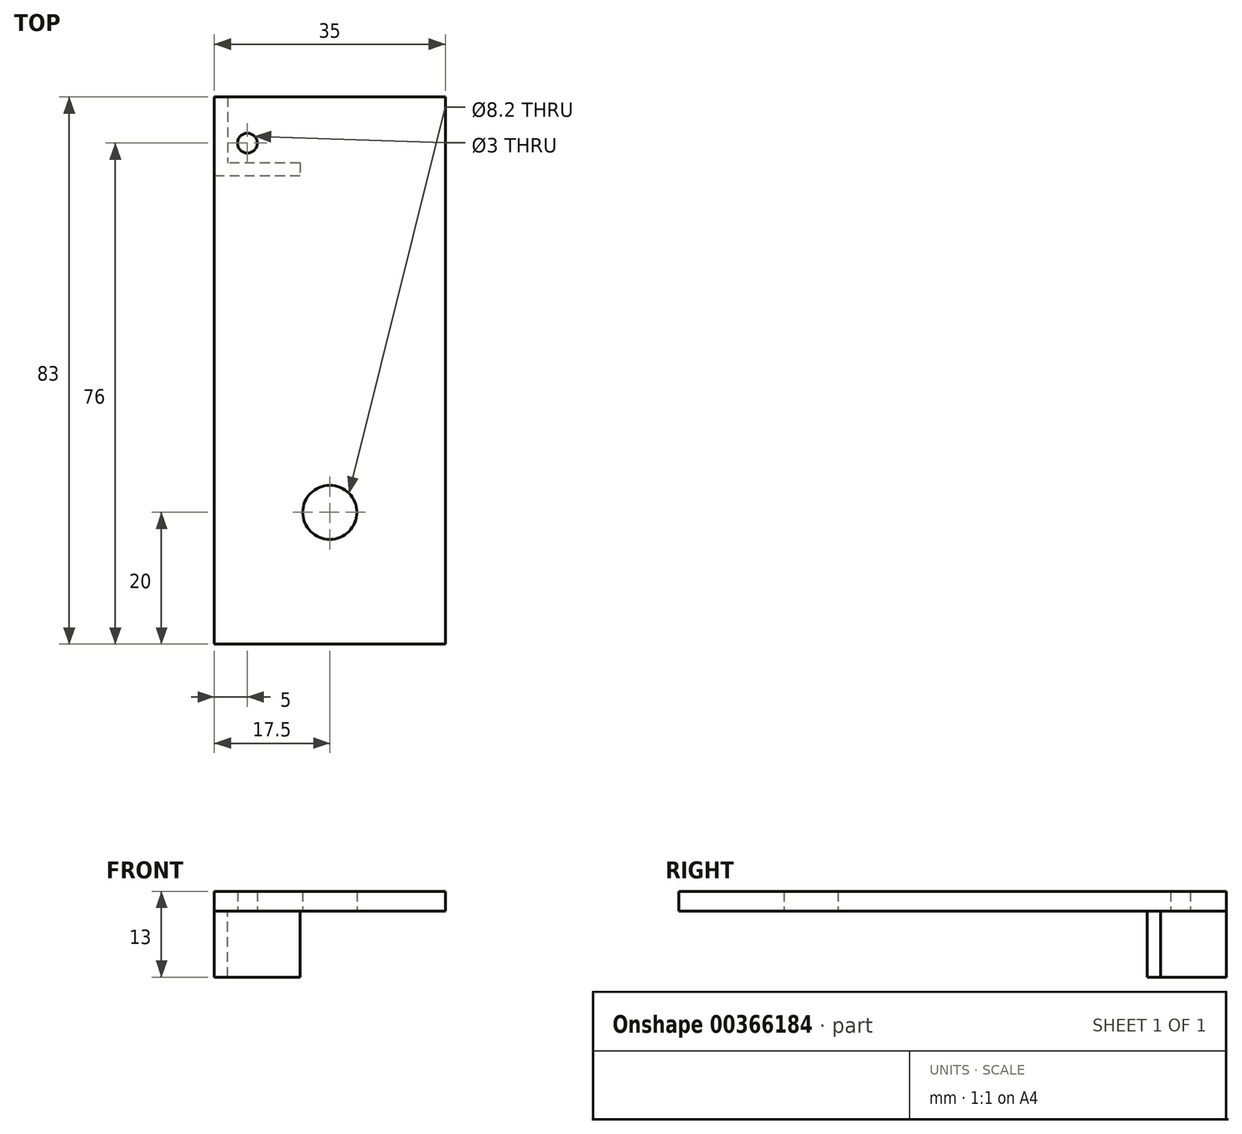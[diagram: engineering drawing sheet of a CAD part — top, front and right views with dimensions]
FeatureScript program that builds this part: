
annotation { "Feature Type Name" : "Feature", "Feature Type Description" : "" }
export const myFeature = defineFeature(function(context is Context, id is Id, definition is map)
    precondition{}
    {
        {
            var Q0;
            Q0=qCreatedBy(makeId("Top.planeOp"),FACE);
            var sketch = newSketch(context, id + "F0", { "sketchPlane" : qUnion([Q0])});
            skLineSegment(sketch, "E0.bottom", {"start": v(-17.5, 41.5) * mm, "end": v(17.5, 41.5) * mm});
            skLineSegment(sketch, "E0.top", {"start": v(-17.5, -41.5) * mm, "end": v(17.5, -41.5) * mm});
            skLineSegment(sketch, "E0.left", {"start": v(-17.5, 41.5) * mm, "end": v(-17.5, -41.5) * mm});
            skLineSegment(sketch, "E0.right", {"start": v(17.5, 41.5) * mm, "end": v(17.5, -41.5) * mm});
            skPoint(sketch, "E0.middle", {"position": v(0, 0) * mm});
            skCircle(sketch, "E1", {"center": v(0, -21.5) * mm, "radius": 4.1 * mm});
            skCircle(sketch, "E2", {"center": v(-12.5, 34.5) * mm, "radius": 1.5 * mm});
            skSolve(sketch);
        }
        {
            var Q0;
            Q0=makeQuery(id+"F0.imprint","IMPRINT",FACE,{"disambiguationData":[TD([[makeQuery(id+"F0.imprint","IMPRINT",EDGE,{"derivedFrom":sQuery(id+"F0.wireOp",EDGE,"E0.bottom")}),-1.0]])]});
            extrude(context, id + "F1", {"entities" : qUnion([Q0]), "depth" : 3 * mm});
        }
        {
            var Q0;
            Q0=makeQuery(id+"F1.opExtrude","CAP_FACE",FACE,{"disambiguationData":[OSD([sQuery(id+"F0.wireOp",EDGE,"E0.bottom"),sQuery(id+"F0.wireOp",EDGE,"E0.top"),sQuery(id+"F0.wireOp",EDGE,"E0.left"),sQuery(id+"F0.wireOp",EDGE,"E0.right"),sQuery(id+"F0.wireOp",EDGE,"E1"),sQuery(id+"F0.wireOp",EDGE,"E2")])],"isStart":true});
            var sketch = newSketch(context, id + "F2", { "sketchPlane" : qUnion([Q0])});
            skLineSegment(sketch, "E3.bottom", {"start": v(-4.5, -31.5) * mm, "end": v(-17.5, -31.5) * mm});
            skLineSegment(sketch, "E3.top", {"start": v(-4.5, -29.5) * mm, "end": v(-17.5, -29.5) * mm});
            skLineSegment(sketch, "E3.left", {"start": v(-4.5, -31.5) * mm, "end": v(-4.5, -29.5) * mm});
            skLineSegment(sketch, "E3.right", {"start": v(-17.5, -31.5) * mm, "end": v(-17.5, -29.5) * mm});
            skLineSegment(sketch, "E4.bottom", {"start": v(-17.5, -41.5) * mm, "end": v(-15.5, -41.5) * mm});
            skLineSegment(sketch, "E4.top", {"start": v(-17.5, -31.5) * mm, "end": v(-15.5, -31.5) * mm});
            skLineSegment(sketch, "E4.left", {"start": v(-17.5, -41.5) * mm, "end": v(-17.5, -31.5) * mm});
            skLineSegment(sketch, "E4.right", {"start": v(-15.5, -41.5) * mm, "end": v(-15.5, -31.5) * mm});
            skSolve(sketch);
        }
        {
            var Q0;
            Q0=makeQuery(id+"F2.imprint","IMPRINT",FACE,{"disambiguationData":[TD([[makeQuery(id+"F2.imprint","IMPRINT",EDGE,{"derivedFrom":sQuery(id+"F2.wireOp",EDGE,"E4.bottom")}),1.0]])]});
            var Q1;
            Q1=makeQuery(id+"F2.imprint","IMPRINT",FACE,{"disambiguationData":[TD([[makeQuery(id+"F2.imprint","IMPRINT",EDGE,{"derivedFrom":sQuery(id+"F2.wireOp",EDGE,"E3.bottom")}),-1.0]])]});
            extrude(context, id + "F3", {"entities" : qUnion([Q0, Q1]), "operationType" : NewBodyOperationType.ADD, "depth" : 10 * mm});
        }
    });
